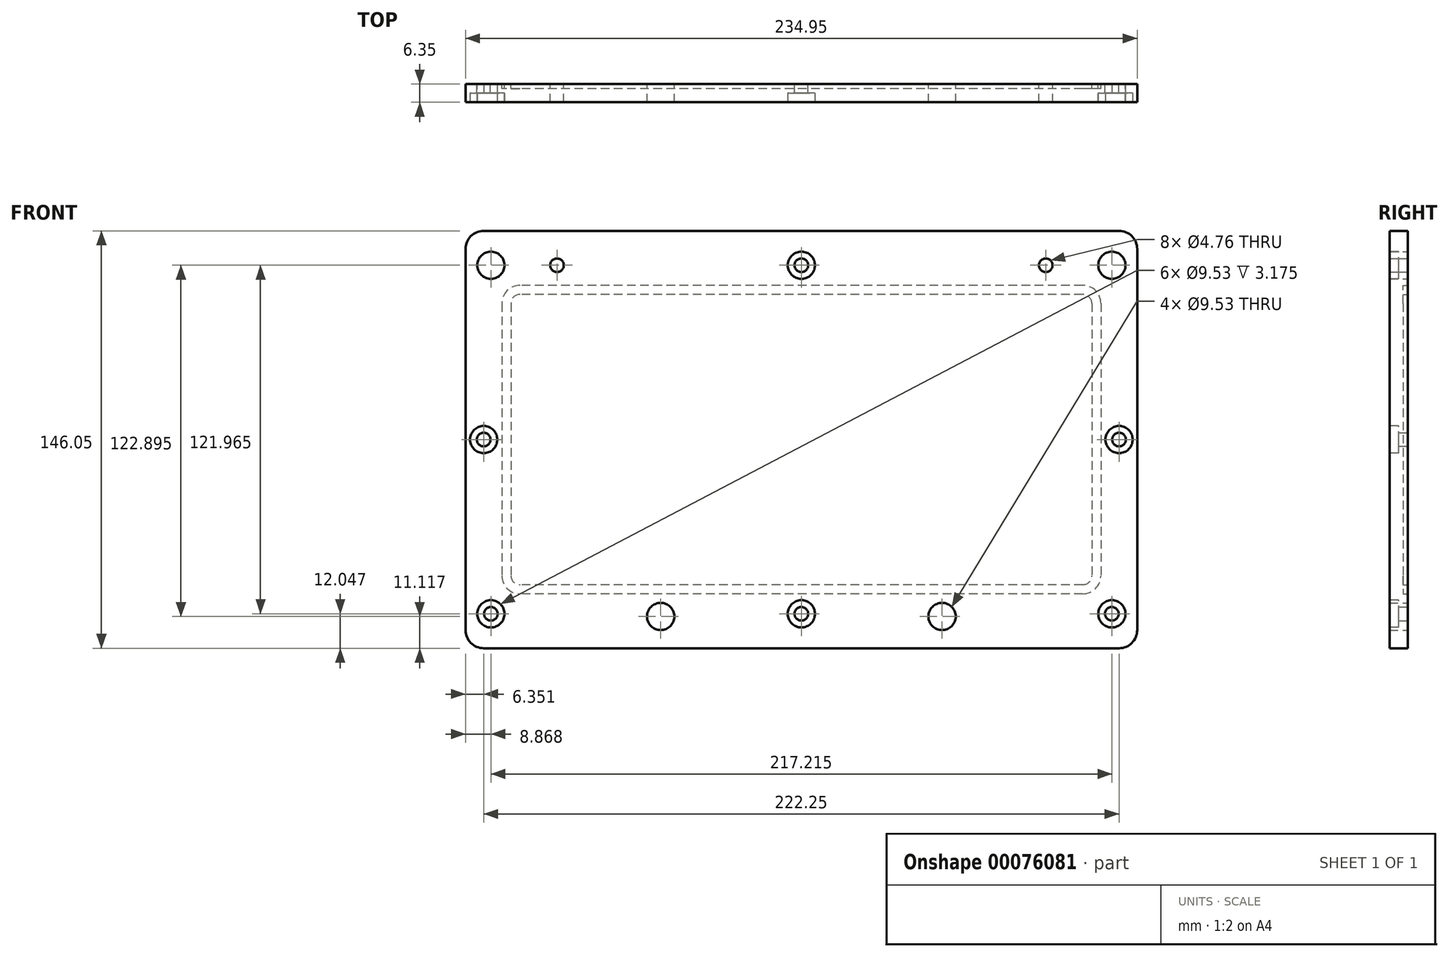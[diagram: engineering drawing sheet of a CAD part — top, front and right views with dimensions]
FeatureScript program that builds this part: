
annotation { "Feature Type Name" : "Feature", "Feature Type Description" : "" }
export const myFeature = defineFeature(function(context is Context, id is Id, definition is map)
    precondition{}
    {
        {
            var Q0;
            Q0=qCreatedBy(makeId("Front.planeOp"),FACE);
            var sketch = newSketch(context, id + "F0", { "sketchPlane" : qUnion([Q0])});
            skPoint(sketch, "E0.visualSharp", {"position": v(-92.06, 54.25) * mm});
            skPoint(sketch, "E1.visualSharp", {"position": v(117.5, 54.25) * mm});
            skPoint(sketch, "E2.visualSharp", {"position": v(117.5, -53.7) * mm});
            skPoint(sketch, "E3.visualSharp", {"position": v(-92.06, -53.7) * mm});
            skLineSegment(sketch, "E4.0", {"start": v(-98.4, 73.3) * mm, "end": v(123.84, 73.3) * mm});
            skLineSegment(sketch, "E5.0", {"start": v(-98.4, -72.75) * mm, "end": v(123.84, -72.75) * mm});
            skLineSegment(sketch, "E6.0", {"start": v(-104.76, 66.95) * mm, "end": v(-104.76, -66.4) * mm});
            skLineSegment(sketch, "E7.0", {"start": v(130.2, 66.95) * mm, "end": v(130.2, -66.4) * mm});
            skPoint(sketch, "E8.visualSharp", {"position": v(-104.76, 73.3) * mm});
            skArc(sketch, "E8.filletArc", {"start": v(-98.4, 73.3) * mm, "mid": v(-102.9, 71.44) * mm, "end": v(-104.76, 66.95) * mm});
            skPoint(sketch, "E9.visualSharp", {"position": v(130.2, 73.3) * mm});
            skArc(sketch, "E9.filletArc", {"start": v(130.2, 66.95) * mm, "mid": v(128.33, 71.44) * mm, "end": v(123.84, 73.3) * mm});
            skPoint(sketch, "E10.visualSharp", {"position": v(130.2, -72.75) * mm});
            skArc(sketch, "E10.filletArc", {"start": v(123.84, -72.75) * mm, "mid": v(128.33, -70.89) * mm, "end": v(130.2, -66.4) * mm});
            skPoint(sketch, "E11.visualSharp", {"position": v(-104.76, -72.75) * mm});
            skArc(sketch, "E11.filletArc", {"start": v(-104.76, -66.4) * mm, "mid": v(-102.9, -70.89) * mm, "end": v(-98.4, -72.75) * mm});
            skLineSegment(sketch, "E12", {"start": v(-104.76, 66.95) * mm, "end": v(-98.4, 73.3) * mm, "construction": true});
            skLineSegment(sketch, "E13", {"start": v(-101.58, 70.13) * mm, "end": v(-90.2, 52.4) * mm, "construction": true});
            skLineSegment(sketch, "E14", {"start": v(-104.76, 0.28) * mm, "end": v(-92.06, 0.28) * mm, "construction": true});
            skLineSegment(sketch, "E15", {"start": v(-98.4, -72.75) * mm, "end": v(-104.76, -66.4) * mm, "construction": true});
            skLineSegment(sketch, "E16", {"start": v(-101.58, -69.57) * mm, "end": v(-90.2, -51.84) * mm, "construction": true});
            skLineSegment(sketch, "E17", {"start": v(12.72, 94.6) * mm, "end": v(12.72, -140.03) * mm, "construction": true});
            skPoint(sketch, "E17.startSnap0", {"position": v(12.72, 73.3) * mm});
            skLineSegment(sketch, "E18", {"start": v(-137.08, 0.28) * mm, "end": v(218.2, 0.28) * mm, "construction": true});
            skLineSegment(sketch, "E19", {"start": v(-85.7, 54.25) * mm, "end": v(-85.7, 73.3) * mm, "construction": true});
            skCircle(sketch, "E20", {"center": v(-95.9, 61.26) * mm, "radius": 4.76 * mm});
            skCircle(sketch, "E21", {"center": v(-98.4, 0.28) * mm, "radius": 2.38 * mm});
            skCircle(sketch, "E22", {"center": v(-95.9, -60.7) * mm, "radius": 2.38 * mm});
            skLineSegment(sketch, "E23", {"start": v(-85.7, -72.75) * mm, "end": v(-85.7, -63.22) * mm, "construction": true});
            skLineSegment(sketch, "E24", {"start": v(12.72, 54.25) * mm, "end": v(12.72, 73.3) * mm, "construction": true});
            skLineSegment(sketch, "E25", {"start": v(12.72, -72.75) * mm, "end": v(12.72, -53.7) * mm, "construction": true});
            skCircle(sketch, "E26", {"center": v(12.72, 61.26) * mm, "radius": 2.38 * mm});
            skPoint(sketch, "E27.middle", {"position": v(-36.5, 62.2) * mm});
            skCircle(sketch, "E28.MirrorC", {"center": v(121.32, 61.26) * mm, "radius": 4.76 * mm});
            skCircle(sketch, "E29.MirrorC", {"center": v(123.84, 0.28) * mm, "radius": 2.38 * mm});
            skCircle(sketch, "E30.MirrorC", {"center": v(121.32, -60.7) * mm, "radius": 2.38 * mm});
            skCircle(sketch, "E31.MirrorC", {"center": v(12.72, -60.7) * mm, "radius": 2.38 * mm});
            skLineSegment(sketch, "E32", {"start": v(-55.55, 62.2) * mm, "end": v(-17.45, 62.2) * mm, "construction": true});
            skLineSegment(sketch, "E33", {"start": v(-36.5, 55.84) * mm, "end": v(-36.5, 68.54) * mm, "construction": true});
            skLineSegment(sketch, "E34", {"start": v(42.88, 62.2) * mm, "end": v(80.98, 62.2) * mm, "construction": true});
            skLineSegment(sketch, "E35", {"start": v(61.93, 55.84) * mm, "end": v(61.93, 68.54) * mm, "construction": true});
            skLineSegment(sketch, "E36", {"start": v(-36.5, -55.28) * mm, "end": v(-36.5, -67.98) * mm, "construction": true});
            skLineSegment(sketch, "E37", {"start": v(-55.55, -61.63) * mm, "end": v(-17.45, -61.63) * mm, "construction": true});
            skLineSegment(sketch, "E38", {"start": v(42.88, -61.63) * mm, "end": v(80.98, -61.63) * mm, "construction": true});
            skLineSegment(sketch, "E39", {"start": v(61.93, -67.98) * mm, "end": v(61.93, -55.28) * mm, "construction": true});
            skCircle(sketch, "E40", {"center": v(-36.5, -61.63) * mm, "radius": 4.76 * mm});
            skCircle(sketch, "E41", {"center": v(61.93, -61.63) * mm, "radius": 4.76 * mm});
            skLineSegment(sketch, "E42", {"start": v(-95.9, 61.26) * mm, "end": v(121.32, 61.26) * mm, "construction": true});
            skCircle(sketch, "E43", {"center": v(-72.76, 61.26) * mm, "radius": 2.38 * mm});
            skCircle(sketch, "E44", {"center": v(98.2, 61.26) * mm, "radius": 2.38 * mm});
            skSolve(sketch);
        }
        {
            var Q0;
            Q0 = qSketchRegion(id + "F0", true);
            extrude(context, id + "F1", {"entities" : qUnion([Q0]), "depth" : 6.35 * mm});
        }
        {
            var Q0;
            Q0=makeQuery(id+"F1.opExtrude","CAP_FACE",FACE,{"disambiguationData":[OSD([sQuery(id+"F0.wireOp",EDGE,"E4.0"),sQuery(id+"F0.wireOp",EDGE,"E5.0"),sQuery(id+"F0.wireOp",EDGE,"E6.0"),sQuery(id+"F0.wireOp",EDGE,"E7.0"),sQuery(id+"F0.wireOp",EDGE,"E8.filletArc"),sQuery(id+"F0.wireOp",EDGE,"E9.filletArc"),sQuery(id+"F0.wireOp",EDGE,"E10.filletArc"),sQuery(id+"F0.wireOp",EDGE,"E11.filletArc"),sQuery(id+"F0.wireOp",EDGE,"E20"),sQuery(id+"F0.wireOp",EDGE,"E21"),sQuery(id+"F0.wireOp",EDGE,"E22"),sQuery(id+"F0.wireOp",EDGE,"E26"),sQuery(id+"F0.wireOp",EDGE,"E28.MirrorC"),sQuery(id+"F0.wireOp",EDGE,"E29.MirrorC"),sQuery(id+"F0.wireOp",EDGE,"E30.MirrorC"),sQuery(id+"F0.wireOp",EDGE,"E31.MirrorC"),sQuery(id+"F0.wireOp",EDGE,"E40"),sQuery(id+"F0.wireOp",EDGE,"E41")])],"isStart":false});
            var sketch = newSketch(context, id + "F2", { "sketchPlane" : qUnion([Q0])});
            skCircle(sketch, "E45", {"center": v(-98.4, 0.28) * mm, "radius": 4.76 * mm});
            skCircle(sketch, "E46", {"center": v(12.72, 61.26) * mm, "radius": 4.76 * mm});
            skCircle(sketch, "E47", {"center": v(123.84, 0.28) * mm, "radius": 4.76 * mm});
            skCircle(sketch, "E48", {"center": v(121.32, -60.7) * mm, "radius": 4.76 * mm});
            skCircle(sketch, "E49", {"center": v(12.72, -60.7) * mm, "radius": 4.76 * mm});
            skCircle(sketch, "E50", {"center": v(-95.9, -60.7) * mm, "radius": 4.76 * mm});
            skSolve(sketch);
        }
        {
            var Q0;
            Q0 = qSketchRegion(id + "F2", true);
            extrude(context, id + "F3", {"entities" : qUnion([Q0]), "operationType" : NewBodyOperationType.REMOVE, "oppositeDirection" : true, "depth" : 3.17 * mm});
        }
        {
            var Q0;
            Q0=makeQuery(id+"F0.imprint","IMPRINT",FACE,{"disambiguationData":[TD([[makeQuery(id+"F0.imprint","IMPRINT",EDGE,{"derivedFrom":sQuery(id+"F0.wireOp",EDGE,"E4.0")}),-1.0]])]});
            var sketch = newSketch(context, id + "F4", { "sketchPlane" : qUnion([Q0])});
            skPoint(sketch, "E51.visualSharp", {"position": v(117.5, 54.25) * mm});
            skArc(sketch, "E51.filletArc", {"start": v(117.5, 47.9) * mm, "mid": v(115.63, 52.4) * mm, "end": v(111.14, 54.25) * mm});
            skPoint(sketch, "E52.visualSharp", {"position": v(-92.06, -53.7) * mm});
            skArc(sketch, "E52.filletArc", {"start": v(-92.06, -47.35) * mm, "mid": v(-90.2, -51.84) * mm, "end": v(-85.7, -53.7) * mm});
            skArc(sketch, "E53.MirrorCS", {"start": v(117.5, -47.35) * mm, "mid": v(115.63, -51.84) * mm, "end": v(111.14, -53.7) * mm});
            skArc(sketch, "E54.MirrorCS", {"start": v(-92.06, 47.9) * mm, "mid": v(-90.2, 52.4) * mm, "end": v(-85.7, 54.25) * mm});
            skLineSegment(sketch, "E55", {"start": v(117.5, 47.9) * mm, "end": v(117.5, -47.35) * mm});
            skLineSegment(sketch, "E56", {"start": v(111.14, -53.7) * mm, "end": v(-85.7, -53.7) * mm});
            skLineSegment(sketch, "E57", {"start": v(111.14, 54.25) * mm, "end": v(-85.7, 54.25) * mm});
            skLineSegment(sketch, "E58", {"start": v(-92.06, 47.9) * mm, "end": v(-92.06, -47.35) * mm});
            skArc(sketch, "E59.0", {"start": v(114.32, 47.9) * mm, "mid": v(113.39, 50.15) * mm, "end": v(111.14, 51.08) * mm});
            skLineSegment(sketch, "E59.1", {"start": v(114.32, 47.9) * mm, "end": v(114.32, -47.35) * mm});
            skLineSegment(sketch, "E59.2", {"start": v(111.14, 51.08) * mm, "end": v(-85.7, 51.08) * mm});
            skArc(sketch, "E59.3", {"start": v(114.32, -47.35) * mm, "mid": v(113.39, -49.6) * mm, "end": v(111.14, -50.52) * mm});
            skArc(sketch, "E59.4", {"start": v(-88.88, 47.9) * mm, "mid": v(-87.95, 50.15) * mm, "end": v(-85.7, 51.08) * mm});
            skLineSegment(sketch, "E59.5", {"start": v(-88.88, 47.9) * mm, "end": v(-88.88, -47.35) * mm});
            skArc(sketch, "E59.6", {"start": v(-88.88, -47.35) * mm, "mid": v(-87.95, -49.6) * mm, "end": v(-85.7, -50.52) * mm});
            skLineSegment(sketch, "E59.7", {"start": v(111.14, -50.52) * mm, "end": v(-85.7, -50.52) * mm});
            skSolve(sketch);
        }
        {
            var Q0;
            Q0 = qSketchRegion(id + "F4", true);
            extrude(context, id + "F5", {"entities" : qUnion([Q0]), "operationType" : NewBodyOperationType.REMOVE, "depth" : 1.59 * mm});
        }
    });
